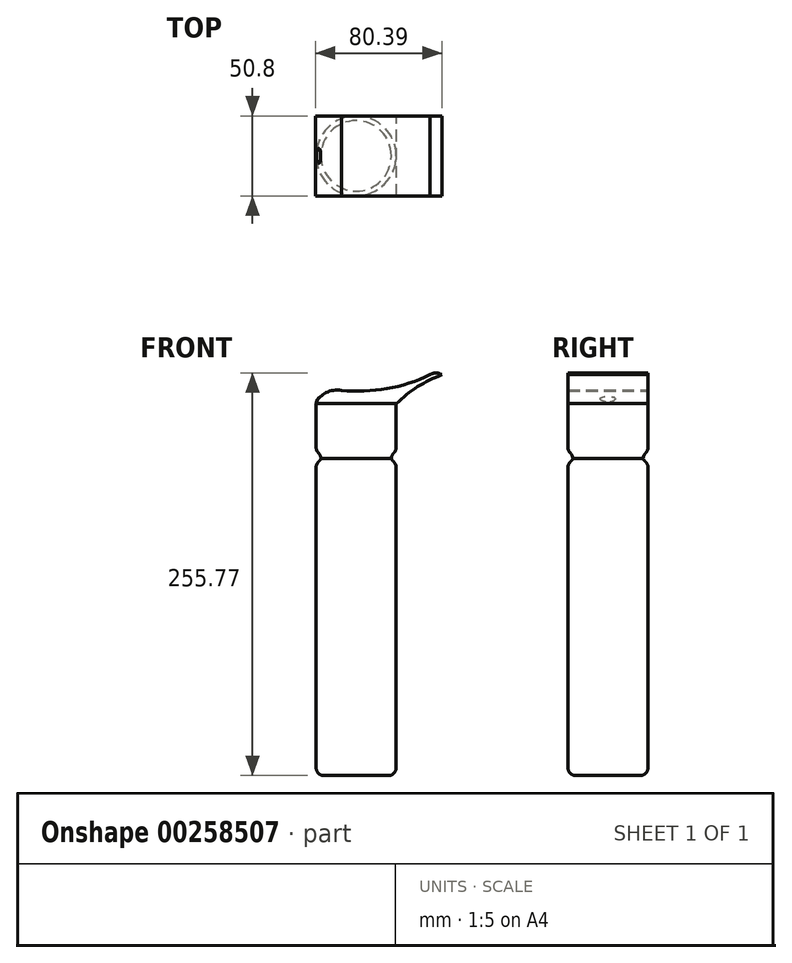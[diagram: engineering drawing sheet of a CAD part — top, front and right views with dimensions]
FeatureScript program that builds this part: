
annotation { "Feature Type Name" : "Feature", "Feature Type Description" : "" }
export const myFeature = defineFeature(function(context is Context, id is Id, definition is map)
    precondition{}
    {
        {
            var Q0;
            Q0=qCreatedBy(makeId("Top.planeOp"),FACE);
            var sketch = newSketch(context, id + "F0", { "sketchPlane" : qUnion([Q0])});
            skCircle(sketch, "E0", {"center": v(0, 0) * mm, "radius": 25.4 * mm});
            skSolve(sketch);
        }
        {
            var Q0;
            Q0=makeQuery(id+"F0.imprint","IMPRINT",FACE,{"disambiguationData":[TD([[makeQuery(id+"F0.imprint","IMPRINT",EDGE,{"derivedFrom":sQuery(id+"F0.wireOp",EDGE,"E0")}),1.0]])]});
            extrude(context, id + "F1", {"entities" : qUnion([Q0]), "oppositeDirection" : true, "depth" : 203.2 * mm});
        }
        {
            var Q0;
            Q0=makeQuery(id+"F1.opExtrude","CAP_EDGE",EDGE,{"disambiguationData":[OSD([sQuery(id+"F0.wireOp",EDGE,"E0")])],"isStart":false});
            fillet(context, id + "F2", {"entities" : qUnion([Q0]), "radius" : 5.08 * mm, "tangentPropagation" : true, "allowEdgeOverflow" : false});
        }
        {
            var Q0;
            Q0=makeQuery(id+"F1.opExtrude","CAP_FACE",FACE,{"disambiguationData":[OSD([sQuery(id+"F0.wireOp",EDGE,"E0")])],"isStart":true});
            extrude(context, id + "F3", {"entities" : qUnion([Q0]), "operationType" : NewBodyOperationType.ADD, "depth" : 38.1 * mm});
        }
        {
            var Q0;
            Q0=qCreatedBy(makeId("Front.planeOp"),FACE);
            var sketch = newSketch(context, id + "F4", { "sketchPlane" : qUnion([Q0])});
            skLineSegment(sketch, "E1.bottom", {"start": v(-32.94, 2.74) * mm, "end": v(-22.37, 2.74) * mm});
            skLineSegment(sketch, "E1.top", {"start": v(-32.94, -2.8) * mm, "end": v(-22.37, -2.8) * mm});
            skLineSegment(sketch, "E1.left", {"start": v(-32.94, 2.74) * mm, "end": v(-32.94, -2.8) * mm});
            skLineSegment(sketch, "E1.right", {"start": v(-22.37, 2.74) * mm, "end": v(-22.37, -2.8) * mm});
            skSolve(sketch);
        }
        {
            var Q0;
            Q0=makeQuery(id+"F4.imprint","IMPRINT",FACE,{"disambiguationData":[TD([[makeQuery(id+"F4.imprint","IMPRINT",EDGE,{"derivedFrom":sQuery(id+"F4.wireOp",EDGE,"E1.bottom")}),-1.0]])]});
            var Q1;
            {var subQ0=sQuery(id+"F0.wireOp",EDGE,"E0");Q1=makeQuery(id+"F3.boolean.opBoolean","MERGE",FACE,{"derivedFrom":[makeQuery(id+"F1.opExtrude","SWEPT_FACE",FACE,{"disambiguationData":[OSD([subQ0])]}),makeQuery(id+"F3.opExtrude","SWEPT_FACE",FACE,{"disambiguationData":[OSD([subQ0])]})]});}
            revolve(context, id + "F5", {"operationType" : NewBodyOperationType.REMOVE, "entities" : qUnion([Q0]), "axis" : qUnion([Q1]), "revolveType" : RevolveType.FULL, "oppositeDirection" : true});
        }
        {
            var Q0;
            Q0=makeQuery(id+"F5.boolean.opBoolean","COPY",EDGE,{"derivedFrom":makeQuery(id+"F5.opRevolve","SWEPT_EDGE",EDGE,{"disambiguationData":[OSD([sQuery(id+"F4.wireOp",EDGE,"E1.bottom"),sQuery(id+"F4.wireOp",EDGE,"E1.right")])]})});
            fillet(context, id + "F6", {"entities" : qUnion([Q0]), "radius" : 5.08 * mm, "tangentPropagation" : true, "allowEdgeOverflow" : false});
        }
        {
            var Q0;
            {var subQ0=sQuery(id+"F0.wireOp",EDGE,"E0");Q0=makeQuery(id+"F5.boolean.opBoolean","INTERSECT",EDGE,{"derivedFrom":[makeQuery(id+"F3.boolean.opBoolean","MERGE",FACE,{"derivedFrom":[makeQuery(id+"F1.opExtrude","SWEPT_FACE",FACE,{"disambiguationData":[OSD([subQ0])]}),makeQuery(id+"F3.opExtrude","SWEPT_FACE",FACE,{"disambiguationData":[OSD([subQ0])]})]}),makeQuery(id+"F5.opRevolve","SWEPT_FACE",FACE,{"disambiguationData":[OSD([sQuery(id+"F4.wireOp",EDGE,"E1.top")])]})]});}
            fillet(context, id + "F7", {"entities" : qUnion([Q0]), "radius" : 5.08 * mm, "tangentPropagation" : true, "allowEdgeOverflow" : false});
        }
        {
            var Q0;
            {var subQ0=sQuery(id+"F0.wireOp",EDGE,"E0");var subQ1=sQuery(id+"F4.wireOp",EDGE,"E1.bottom");Q0=makeQuery(id+"F6.opFillet","BLEND_EDGE",EDGE,{"blendedFrom":[makeQuery(id+"F5.boolean.opBoolean","COPY",EDGE,{"derivedFrom":makeQuery(id+"F5.opRevolve","SWEPT_EDGE",EDGE,{"disambiguationData":[OSD([subQ1,sQuery(id+"F4.wireOp",EDGE,"E1.right")])]})}),makeQuery(id+"F5.boolean.opBoolean","SPLIT",FACE,{"disambiguationData":[TD([makeQuery(id+"F3.opExtrude","CAP_FACE",FACE,{"disambiguationData":[OSD([subQ0])],"isStart":false})])],"derivedFrom":makeQuery(id+"F3.boolean.opBoolean","MERGE",FACE,{"derivedFrom":[makeQuery(id+"F1.opExtrude","SWEPT_FACE",FACE,{"disambiguationData":[OSD([subQ0])]}),makeQuery(id+"F3.opExtrude","SWEPT_FACE",FACE,{"disambiguationData":[OSD([subQ0])]})]})})],"blendedInto":[makeQuery(id+"F5.boolean.opBoolean","SPLIT",FACE,{"disambiguationData":[TD([makeQuery(id+"F3.opExtrude","CAP_FACE",FACE,{"disambiguationData":[OSD([subQ0])],"isStart":false})])],"derivedFrom":makeQuery(id+"F3.boolean.opBoolean","MERGE",FACE,{"derivedFrom":[makeQuery(id+"F1.opExtrude","SWEPT_FACE",FACE,{"disambiguationData":[OSD([subQ0])]}),makeQuery(id+"F3.opExtrude","SWEPT_FACE",FACE,{"disambiguationData":[OSD([subQ0])]})]})})]});}
            var Q1;
            {var subQ0=sQuery(id+"F0.wireOp",EDGE,"E0");Q1=makeQuery(id+"F7.opFillet","BLEND_EDGE",EDGE,{"blendedFrom":[makeQuery(id+"F5.boolean.opBoolean","INTERSECT",EDGE,{"derivedFrom":[makeQuery(id+"F3.boolean.opBoolean","MERGE",FACE,{"derivedFrom":[makeQuery(id+"F1.opExtrude","SWEPT_FACE",FACE,{"disambiguationData":[OSD([subQ0])]}),makeQuery(id+"F3.opExtrude","SWEPT_FACE",FACE,{"disambiguationData":[OSD([subQ0])]})]}),makeQuery(id+"F5.opRevolve","SWEPT_FACE",FACE,{"disambiguationData":[OSD([sQuery(id+"F4.wireOp",EDGE,"E1.top")])]})]}),makeQuery(id+"F5.boolean.opBoolean","COPY",FACE,{"derivedFrom":makeQuery(id+"F5.opRevolve","SWEPT_FACE",FACE,{"disambiguationData":[OSD([sQuery(id+"F4.wireOp",EDGE,"E1.right")])]})})],"blendedInto":[makeQuery(id+"F5.boolean.opBoolean","COPY",FACE,{"derivedFrom":makeQuery(id+"F5.opRevolve","SWEPT_FACE",FACE,{"disambiguationData":[OSD([sQuery(id+"F4.wireOp",EDGE,"E1.right")])]})})]});}
            var Q2;
            Q2=makeQuery(id+"F3.opExtrude","CAP_EDGE",EDGE,{"disambiguationData":[OSD([sQuery(id+"F0.wireOp",EDGE,"E0")])],"isStart":false});
            fillet(context, id + "F8", {"entities" : qUnion([Q0, Q1, Q2]), "radius" : 5.08 * mm, "tangentPropagation" : true, "allowEdgeOverflow" : false});
        }
        {
            var Q0;
            Q0=qCreatedBy(makeId("Front.planeOp"),FACE);
            var sketch = newSketch(context, id + "F9", { "sketchPlane" : qUnion([Q0])});
            skLineSegment(sketch, "E2", {"start": v(-25.82, 33.09) * mm, "end": v(25.54, 33.09) * mm});
            skArc(sketch, "E3", {"start": v(54.57, 51.43) * mm, "mid": v(39.09, 43.8) * mm, "end": v(25.54, 33.09) * mm});
            skArc(sketch, "E4", {"start": v(54.57, 51.43) * mm, "mid": v(50.83, 52.57) * mm, "end": v(47.08, 51.43) * mm});
            skArc(sketch, "E5", {"start": v(-9.39, 41.54) * mm, "mid": v(19.53, 42.59) * mm, "end": v(47.08, 51.43) * mm});
            skArc(sketch, "E6", {"start": v(-9.39, 41.54) * mm, "mid": v(-19.01, 40.05) * mm, "end": v(-25.82, 33.09) * mm});
            skSolve(sketch);
        }
        {
            var Q0;
            Q0=makeQuery(id+"F9.imprint","IMPRINT",FACE,{"disambiguationData":[TD([[makeQuery(id+"F9.imprint","IMPRINT",EDGE,{"derivedFrom":sQuery(id+"F9.wireOp",EDGE,"E2")}),1.0]])]});
            extrude(context, id + "F10", {"entities" : qUnion([Q0]), "operationType" : NewBodyOperationType.ADD, "endBound" : BoundingType.SYMMETRIC, "depth" : 50.8 * mm});
        }
    });
